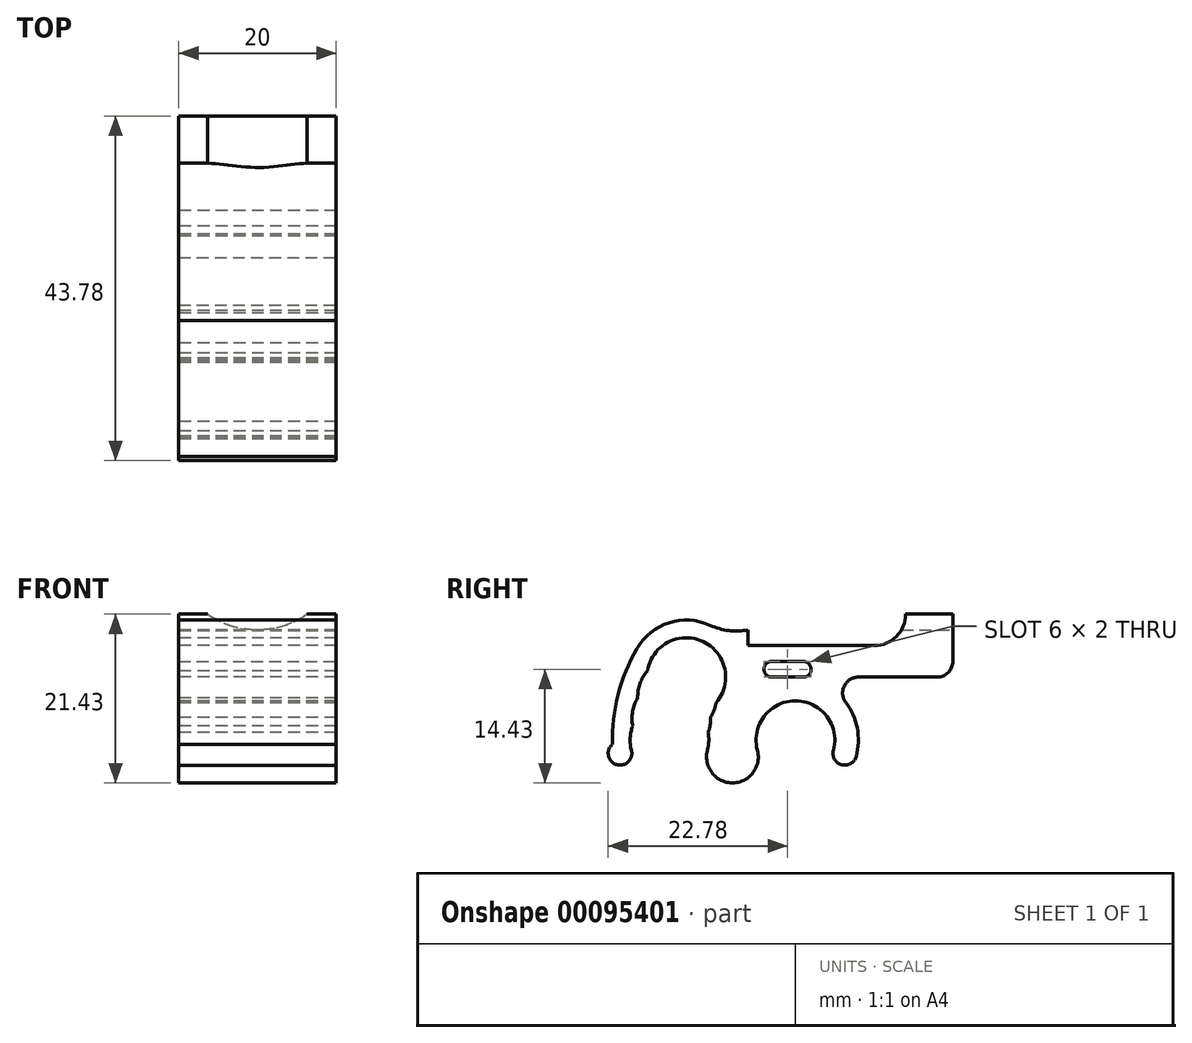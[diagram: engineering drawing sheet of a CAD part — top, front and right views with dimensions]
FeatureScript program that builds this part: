
annotation { "Feature Type Name" : "Feature", "Feature Type Description" : "" }
export const myFeature = defineFeature(function(context is Context, id is Id, definition is map)
    precondition{}
    {
        {
            var Q0;
            Q0=qCreatedBy(makeId("Right.planeOp"),FACE);
            var sketch = newSketch(context, id + "F0", { "sketchPlane" : qUnion([Q0])});
            skCircle(sketch, "E0", {"center": v(0, 0) * mm, "radius": 3.97 * mm, "construction": true});
            skCircle(sketch, "E1", {"center": v(-16, 0) * mm, "radius": 3.97 * mm, "construction": true});
            skCircle(sketch, "E2", {"center": v(0, 0) * mm, "radius": 16 * mm, "construction": true});
            skLineSegment(sketch, "E3", {"start": v(0, 0) * mm, "end": v(-13.86, 8) * mm, "construction": true});
            skLineSegment(sketch, "E4", {"start": v(0, 0) * mm, "end": v(-15.04, 5.47) * mm, "construction": true});
            skLineSegment(sketch, "E5", {"start": v(0, 0) * mm, "end": v(-15.76, 2.78) * mm, "construction": true});
            skArc(sketch, "E6", {"start": v(-20.66, 1.8) * mm, "mid": v(-21, 0.27) * mm, "end": v(-20.83, -1.3) * mm});
            skArc(sketch, "E7", {"start": v(-20.03, 5.37) * mm, "mid": v(-20.68, 3.65) * mm, "end": v(-20.66, 1.8) * mm});
            skArc(sketch, "E8", {"start": v(-18.8, 8.77) * mm, "mid": v(-19.73, 7.18) * mm, "end": v(-20.03, 5.37) * mm});
            skArc(sketch, "E9", {"start": v(4.83, -1.3) * mm, "mid": v(0, 5) * mm, "end": v(-4.83, -1.3) * mm});
            skArc(sketch, "E10.trimOffspring", {"start": v(-10.1, 4.7) * mm, "mid": v(-11.74, 12.53) * mm, "end": v(-18.8, 8.77) * mm});
            skArc(sketch, "E11.trimOffspring", {"start": v(-10.76, 2.88) * mm, "mid": v(-10.34, 3.76) * mm, "end": v(-10.1, 4.7) * mm});
            skArc(sketch, "E12.trimOffspring", {"start": v(-11.1, 0.97) * mm, "mid": v(-10.83, 1.91) * mm, "end": v(-10.76, 2.88) * mm});
            skLineSegment(sketch, "E13", {"start": v(-16, 0) * mm, "end": v(-25.66, -2.59) * mm, "construction": true});
            skLineSegment(sketch, "E14", {"start": v(-16, 0) * mm, "end": v(-6.34, -2.59) * mm, "construction": true});
            skArc(sketch, "E15", {"start": v(7.73, -2.07) * mm, "mid": v(7.85, 1.52) * mm, "end": v(6.4, 4.8) * mm});
            skArc(sketch, "E16", {"start": v(-20.14, 11.62) * mm, "mid": v(-22.53, 5.76) * mm, "end": v(-23.24, -0.53) * mm});
            skPoint(sketch, "E17.start.orphan", {"position": v(0, -8) * mm});
            skArc(sketch, "E18.trimOffspring", {"start": v(-10.83, 14.59) * mm, "mid": v(-16.06, 14.9) * mm, "end": v(-20.14, 11.62) * mm});
            skArc(sketch, "E19", {"start": v(-23.24, -0.53) * mm, "mid": v(-22.73, -3.11) * mm, "end": v(-20.83, -1.3) * mm});
            skArc(sketch, "E20.trimOffspring", {"start": v(-11.17, -1.3) * mm, "mid": v(-11, -0.17) * mm, "end": v(-11.1, 0.97) * mm});
            skArc(sketch, "E21", {"start": v(-11.17, -1.3) * mm, "mid": v(-8, -5.43) * mm, "end": v(-4.83, -1.3) * mm});
            skLineSegment(sketch, "E22", {"start": v(-4.83, -1.3) * mm, "end": v(4.83, -1.3) * mm, "construction": true});
            skArc(sketch, "E23", {"start": v(4.83, -1.3) * mm, "mid": v(5.9, -3.13) * mm, "end": v(7.73, -2.07) * mm});
            skLineSegment(sketch, "E24", {"start": v(0, 0) * mm, "end": v(0, 16) * mm, "construction": true});
            skLineSegment(sketch, "E25", {"start": v(-6, 12) * mm, "end": v(-6, 14) * mm});
            skLineSegment(sketch, "E26", {"start": v(-6, 12) * mm, "end": v(10, 12) * mm});
            skLineSegment(sketch, "E27", {"start": v(20, 16) * mm, "end": v(14, 16) * mm});
            skLineSegment(sketch, "E28", {"start": v(20, 16) * mm, "end": v(20, 10) * mm});
            skArc(sketch, "E29", {"start": v(-10.83, 14.59) * mm, "mid": v(-8.46, 13.92) * mm, "end": v(-6, 14) * mm});
            skArc(sketch, "E30", {"start": v(10, 12) * mm, "mid": v(12.83, 13.17) * mm, "end": v(14, 16) * mm});
            skLineSegment(sketch, "E31", {"start": v(18, 8) * mm, "end": v(8, 8) * mm});
            skPoint(sketch, "E32.visualSharp", {"position": v(20, 8) * mm});
            skArc(sketch, "E32.filletArc", {"start": v(18, 8) * mm, "mid": v(19.41, 8.59) * mm, "end": v(20, 10) * mm});
            skArc(sketch, "E33", {"start": v(8, 8) * mm, "mid": v(6.21, 6.9) * mm, "end": v(6.4, 4.8) * mm});
            skSolve(sketch);
        }
        {
            var Q0;
            Q0 = qSketchRegion(id + "F0", true);
            extrude(context, id + "F1", {"entities" : qUnion([Q0]), "endBound" : BoundingType.SYMMETRIC, "depth" : 20 * mm});
        }
        {
            var Q0;
            Q0=makeQuery(id+"F1.opExtrude","CAP_FACE",FACE,{"disambiguationData":[OSD([sQuery(id+"F0.wireOp",EDGE,"E6"),sQuery(id+"F0.wireOp",EDGE,"E7"),sQuery(id+"F0.wireOp",EDGE,"E8"),sQuery(id+"F0.wireOp",EDGE,"E9"),sQuery(id+"F0.wireOp",EDGE,"E10.trimOffspring"),sQuery(id+"F0.wireOp",EDGE,"E11.trimOffspring"),sQuery(id+"F0.wireOp",EDGE,"E12.trimOffspring"),sQuery(id+"F0.wireOp",EDGE,"E15"),sQuery(id+"F0.wireOp",EDGE,"E16"),sQuery(id+"F0.wireOp",EDGE,"E18.trimOffspring"),sQuery(id+"F0.wireOp",EDGE,"E19"),sQuery(id+"F0.wireOp",EDGE,"E20.trimOffspring"),sQuery(id+"F0.wireOp",EDGE,"E21"),sQuery(id+"F0.wireOp",EDGE,"E23"),sQuery(id+"F0.wireOp",EDGE,"E25"),sQuery(id+"F0.wireOp",EDGE,"E26"),sQuery(id+"F0.wireOp",EDGE,"E27"),sQuery(id+"F0.wireOp",EDGE,"E28"),sQuery(id+"F0.wireOp",EDGE,"E29"),sQuery(id+"F0.wireOp",EDGE,"E30"),sQuery(id+"F0.wireOp",EDGE,"E31"),sQuery(id+"F0.wireOp",EDGE,"E32.filletArc"),sQuery(id+"F0.wireOp",EDGE,"E33")])],"isStart":false});
            var sketch = newSketch(context, id + "F2", { "sketchPlane" : qUnion([Q0])});
            skLineSegment(sketch, "E34", {"start": v(-3, 10) * mm, "end": v(1, 10) * mm});
            skLineSegment(sketch, "E35", {"start": v(-3, 8) * mm, "end": v(1, 8) * mm});
            skArc(sketch, "E36", {"start": v(-3, 10) * mm, "mid": v(-4, 9) * mm, "end": v(-3, 8) * mm});
            skArc(sketch, "E37", {"start": v(1, 8) * mm, "mid": v(2, 9) * mm, "end": v(1, 10) * mm});
            skSolve(sketch);
        }
        {
            var Q0;
            Q0 = qSketchRegion(id + "F2", true);
            var Q1;
            Q1=makeQuery(id+"F1.opExtrude","CAP_FACE",FACE,{"disambiguationData":[OSD([sQuery(id+"F0.wireOp",EDGE,"E6"),sQuery(id+"F0.wireOp",EDGE,"E7"),sQuery(id+"F0.wireOp",EDGE,"E8"),sQuery(id+"F0.wireOp",EDGE,"E9"),sQuery(id+"F0.wireOp",EDGE,"E10.trimOffspring"),sQuery(id+"F0.wireOp",EDGE,"E11.trimOffspring"),sQuery(id+"F0.wireOp",EDGE,"E12.trimOffspring"),sQuery(id+"F0.wireOp",EDGE,"E15"),sQuery(id+"F0.wireOp",EDGE,"E16"),sQuery(id+"F0.wireOp",EDGE,"E18.trimOffspring"),sQuery(id+"F0.wireOp",EDGE,"E19"),sQuery(id+"F0.wireOp",EDGE,"E20.trimOffspring"),sQuery(id+"F0.wireOp",EDGE,"E21"),sQuery(id+"F0.wireOp",EDGE,"E23"),sQuery(id+"F0.wireOp",EDGE,"E25"),sQuery(id+"F0.wireOp",EDGE,"E26"),sQuery(id+"F0.wireOp",EDGE,"E27"),sQuery(id+"F0.wireOp",EDGE,"E28"),sQuery(id+"F0.wireOp",EDGE,"E29"),sQuery(id+"F0.wireOp",EDGE,"E30"),sQuery(id+"F0.wireOp",EDGE,"E31"),sQuery(id+"F0.wireOp",EDGE,"E32.filletArc"),sQuery(id+"F0.wireOp",EDGE,"E33")])],"isStart":true});
            extrude(context, id + "F3", {"entities" : qUnion([Q0]), "operationType" : NewBodyOperationType.REMOVE, "endBound" : BoundingType.UP_TO_SURFACE, "oppositeDirection" : true, "endBoundEntityFace" : qUnion([Q1]), "depth" : 25 * mm});
        }
        {
            var Q0;
            Q0=makeQuery(id+"F1.opExtrude","SWEPT_FACE",FACE,{"disambiguationData":[OSD([sQuery(id+"F0.wireOp",EDGE,"E28")])]});
            var sketch = newSketch(context, id + "F4", { "sketchPlane" : qUnion([Q0])});
            skLineSegment(sketch, "E38", {"start": v(0, 10) * mm, "end": v(0, 25) * mm, "construction": true});
            skPoint(sketch, "E38.endSnap0", {"position": v(0, 10) * mm});
            skArc(sketch, "E39", {"start": v(-6.32, 16) * mm, "mid": v(0, 14) * mm, "end": v(6.32, 16) * mm});
            skLineSegment(sketch, "E40", {"start": v(-6.32, 16) * mm, "end": v(6.32, 16) * mm});
            skSolve(sketch);
        }
        {
            var Q0;
            Q0 = qSketchRegion(id + "F4", true);
            var Q1;
            Q1=makeQuery(id+"F1.opExtrude","SWEPT_FACE",FACE,{"disambiguationData":[OSD([sQuery(id+"F0.wireOp",EDGE,"E30")])]});
            extrude(context, id + "F5", {"entities" : qUnion([Q0]), "operationType" : NewBodyOperationType.REMOVE, "endBound" : BoundingType.UP_TO_SURFACE, "oppositeDirection" : true, "endBoundEntityFace" : qUnion([Q1]), "depth" : 25 * mm});
        }
    });
